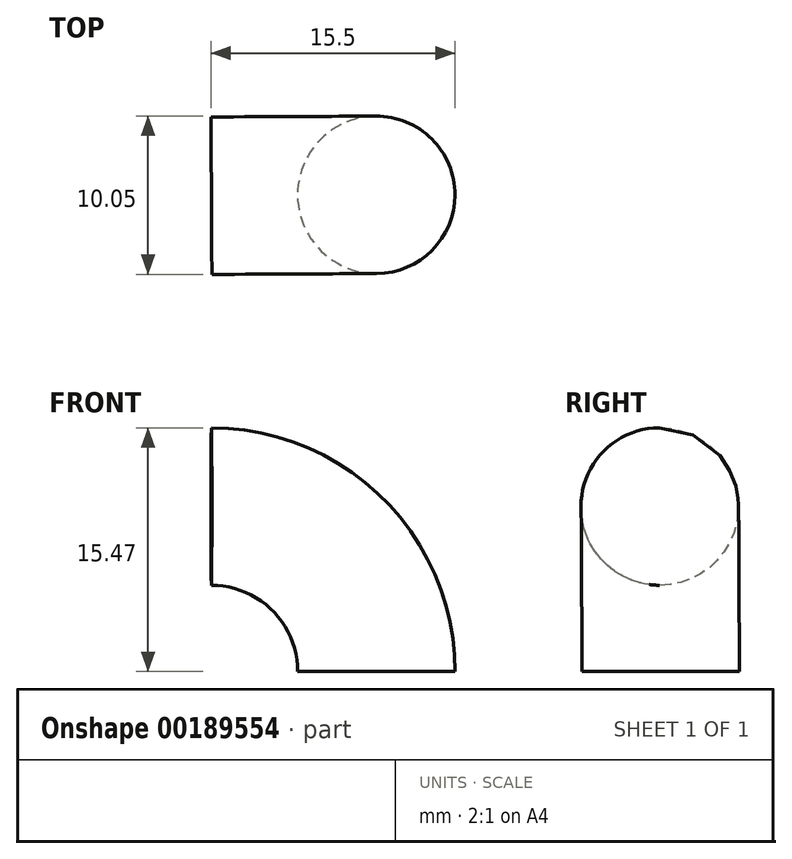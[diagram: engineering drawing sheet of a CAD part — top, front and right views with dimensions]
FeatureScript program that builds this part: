
annotation { "Feature Type Name" : "Feature", "Feature Type Description" : "" }
export const myFeature = defineFeature(function(context is Context, id is Id, definition is map)
    precondition{}
    {
        {
            var Q0;
            Q0=qCreatedBy(makeId("Top.planeOp"),FACE);
            var sketch = newSketch(context, id + "F0", { "sketchPlane" : qUnion([Q0])});
            skCircle(sketch, "E0", {"center": v(0, 0) * mm, "radius": 5 * mm});
            skSolve(sketch);
        }
        {
            var Q0;
            Q0=qCreatedBy(makeId("Top.planeOp"),FACE);
            var sketch = newSketch(context, id + "F1", { "sketchPlane" : qUnion([Q0])});
            skLineSegment(sketch, "E1", {"start": v(0, 0) * mm, "end": v(-10.2, 0) * mm});
            skLineSegment(sketch, "E2", {"start": v(-10.58, 21.77) * mm, "end": v(-10.2, -52.13) * mm});
            skSolve(sketch);
        }
        {
            var Q0;
            Q0=makeQuery(id+"F0.imprint","IMPRINT",FACE,{"disambiguationData":[TD([[makeQuery(id+"F0.imprint","IMPRINT",EDGE,{"derivedFrom":sQuery(id+"F0.wireOp",EDGE,"E0")}),1.0]])]});
            var Q1;
            Q1=sQuery(id+"F1.wireOp",EDGE,"E2");
            revolve(context, id + "F2", {"entities" : qUnion([Q0]), "axis" : qUnion([Q1]), "revolveType" : RevolveType.ONE_DIRECTION, "angle" : 90 * degree});
        }
    });
